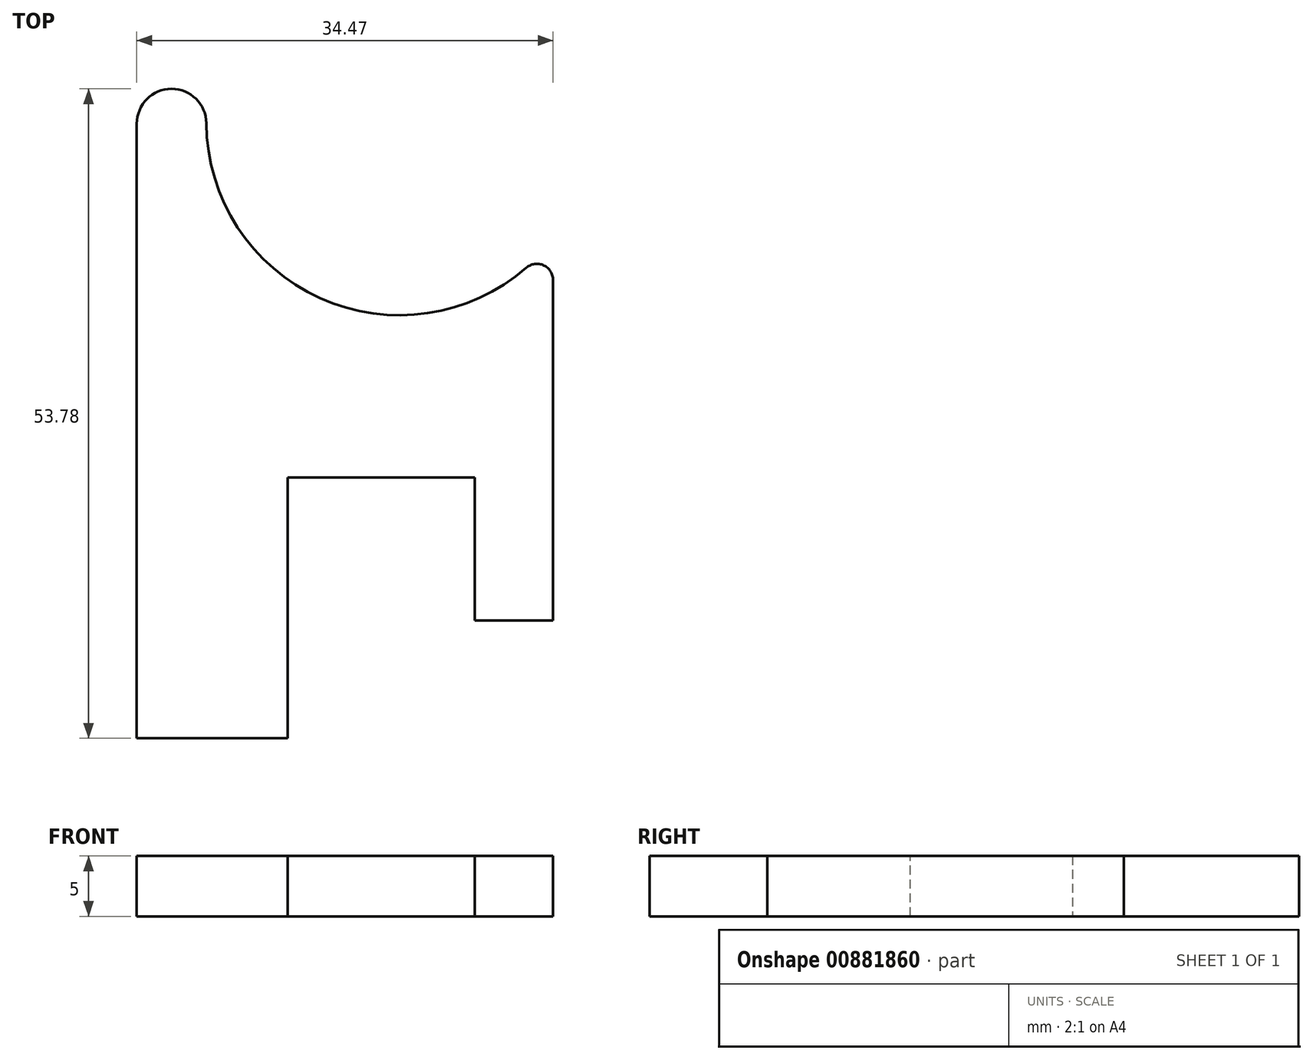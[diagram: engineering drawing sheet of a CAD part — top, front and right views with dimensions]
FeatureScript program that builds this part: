
annotation { "Feature Type Name" : "Feature", "Feature Type Description" : "" }
export const myFeature = defineFeature(function(context is Context, id is Id, definition is map)
    precondition{}
    {
        {
            var Q0;
            Q0=qCreatedBy(makeId("Top.planeOp"),FACE);
            var sketch = newSketch(context, id + "F0", { "sketchPlane" : qUnion([Q0])});
            skLineSegment(sketch, "E0.bottom", {"start": v(0, 0) * mm, "end": v(34.47, 0) * mm});
            skLineSegment(sketch, "E0.left", {"start": v(0, 0) * mm, "end": v(0, 29.3) * mm});
            skLineSegment(sketch, "E0.right", {"start": v(34.47, 0) * mm, "end": v(34.47, 16.35) * mm});
            skArc(sketch, "E1", {"start": v(5.76, 29.32) * mm, "mid": v(15.17, 14.85) * mm, "end": v(32.26, 17.36) * mm});
            skCircle(sketch, "E2", {"center": v(33.13, 16.35) * mm, "radius": 1.34 * mm});
            skCircle(sketch, "E3", {"center": v(2.88, 29.3) * mm, "radius": 2.88 * mm});
            skSolve(sketch);
        }
        {
            var Q0;
            Q0=qSketchRegion(id+"F0",true);
            extrude(context, id + "F1", {"entities" : qUnion([Q0]), "depth" : 5 * mm, "offsetDistance" : 25 * mm});
        }
        {
            var Q0;
            Q0=makeQuery(id+"F1.opExtrude","CAP_FACE",FACE,{"disambiguationData":[OSD([sQuery(id+"F0.wireOp",EDGE,"E0.bottom"),sQuery(id+"F0.wireOp",EDGE,"E0.left"),sQuery(id+"F0.wireOp",EDGE,"E0.right"),sQuery(id+"F0.wireOp",EDGE,"E1"),sQuery(id+"F0.wireOp",EDGE,"E2"),sQuery(id+"F0.wireOp",EDGE,"E3")])],"isStart":false});
            var sketch = newSketch(context, id + "F2", { "sketchPlane" : qUnion([Q0])});
            skLineSegment(sketch, "E4", {"start": v(34.47, 0) * mm, "end": v(34.47, -11.86) * mm});
            skLineSegment(sketch, "E5", {"start": v(34.47, -11.86) * mm, "end": v(0, -11.86) * mm});
            skLineSegment(sketch, "E6", {"start": v(0, -11.86) * mm, "end": v(0, 0) * mm});
            skLineSegment(sketch, "E7", {"start": v(0, 25.4) * mm, "end": v(0, 0) * mm});
            skLineSegment(sketch, "E8", {"start": v(0, 0) * mm, "end": v(28, 0) * mm, "construction": true});
            skLineSegment(sketch, "E9", {"start": v(28, 0) * mm, "end": v(28, -11.86) * mm});
            skLineSegment(sketch, "E10", {"start": v(28, 0) * mm, "end": v(0, 0) * mm});
            skLineSegment(sketch, "E11", {"start": v(12.5, 0) * mm, "end": v(12.5, -21.6) * mm});
            skLineSegment(sketch, "E12", {"start": v(12.5, -21.6) * mm, "end": v(0, -21.6) * mm});
            skLineSegment(sketch, "E13", {"start": v(0, -21.6) * mm, "end": v(0, 0) * mm});
            skSolve(sketch);
        }
        {
            var Q0;
            {var subQ0=makeQuery(id+"F1.opExtrude","CAP_EDGE",EDGE,{"disambiguationData":[OSD([sQuery(id+"F0.wireOp",EDGE,"E0.bottom")])],"isStart":false});Q0=makeQuery(id+"F2.imprint","IMPRINT",FACE,{"disambiguationData":[TD([[makeQuery(id+"F2.imprint","IMPRINT",EDGE,{"derivedFrom":subQ0}),1.0]])]});}
            var Q1;
            Q1=makeQuery(id+"F2.imprint","IMPRINT",FACE,{"disambiguationData":[TD([[makeQuery(id+"F2.imprint","IMPRINT",EDGE,{"derivedFrom":sQuery(id+"F2.wireOp",EDGE,"E4")}),-1.0]])]});
            var Q2;
            {var subQ0=sQuery(id+"F2.wireOp",EDGE,"irv26uyZ-Q05m-Obbf-i6gP-vnwM5PRfqptf");Q2=makeQuery(id+"F2.imprint","IMPRINT",FACE,{"disambiguationData":[TD([[makeQuery(id+"F2.imprint","IMPRINT",EDGE,{"derivedFrom":subQ0}),-1.0]])]});}
            var Q3;
            Q3=makeQuery(id+"F2.imprint","IMPRINT",FACE,{"disambiguationData":[TD([[makeQuery(id+"F2.imprint","IMPRINT",EDGE,{"derivedFrom":sQuery(id+"F2.wireOp",EDGE,"E6")}),1.0]])]});
            var Q4;
            Q4=makeQuery(id+"F2.imprint","IMPRINT",FACE,{"disambiguationData":[TD([[makeQuery(id+"F2.imprint","IMPRINT",EDGE,{"derivedFrom":sQuery(id+"F2.wireOp",EDGE,"ofJB3Zwj-cb0b-pxFX-ohRY-9smDkkZWKUw9")}),-1.0]])]});
            var Q5;
            Q5=makeQuery(id+"F2.imprint","IMPRINT",FACE,{"disambiguationData":[TD([[makeQuery(id+"F2.imprint","IMPRINT",EDGE,{"derivedFrom":sQuery(id+"F2.wireOp",EDGE,"n5eKajka-dC8S-4JBB-TwKA-MAq4kMRF0Qyh")}),1.0]])]});
            var Q6;
            {var subQ5=sQuery(id+"F2.wireOp",EDGE,"E12");Q6=makeQuery(id+"F2.imprint","IMPRINT",FACE,{"disambiguationData":[TD([[makeQuery(id+"F2.imprint","IMPRINT",EDGE,{"derivedFrom":subQ5}),-1.0]])]});}
            var Q7;
            {var subQ0=sQuery(id+"F2.wireOp",EDGE,"E13");var subQ1=sQuery(id+"F2.wireOp",EDGE,"E5");var subQ2=makeQuery(id+"F2.imprint","INTERSECT",VERTEX,{"derivedFrom":[subQ1,subQ0]});Q7=makeQuery(id+"F2.imprint","IMPRINT",FACE,{"disambiguationData":[TD([[makeQuery(id+"F2.imprint","IMPRINT",EDGE,{"disambiguationData":[TD([[subQ2,1.0]])],"derivedFrom":subQ1}),-1.0]])]});}
            extrude(context, id + "F3", {"entities" : qUnion([Q0, Q1, Q2, Q3, Q4, Q5, Q6, Q7]), "operationType" : NewBodyOperationType.ADD, "oppositeDirection" : true, "depth" : 5 * mm, "offsetDistance" : 25 * mm});
        }
    });
